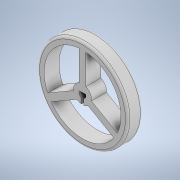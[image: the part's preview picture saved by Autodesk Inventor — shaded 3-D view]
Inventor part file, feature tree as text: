
AUTODESK INVENTOR PART (.ipt)
format: ipt  version: 2022.2 (Build 262287010, 287A)  size: 186,880 bytes
history: native  units: mm
features: extrude x4, sketch x4, fillet x1
ambient origin geometry x8: Origin, YZ Plane, XZ Plane, XY Plane, X Axis, Y Axis, Z Axis, Center Point
bodies: Solid1 (feature_tree)
feature tree (9):
  extrude  "Extrusion1"  Depth=6.6mm TaperAngle=0.0deg
  extrude  "Extrusion3"  TaperAngle=120.0deg  [1 undecoded]
  extrude  "Extrusion5"  Depth=1.5mm
  extrude  "Extrusion6"  Depth=1.5mm
  fillet  "Arredondamento1"  Radius=1.5mm
  sketch  "Sketch1"  dims[d0=40.0mm d1=6.6mm d2=0.0mm]
  sketch  "Sketch3"  dims[d6=34.0mm d7=120.0deg]
  sketch  "Sketch5"  dims[d8=150.0deg d9=1.5mm]
  sketch  "Sketch6"  dims[d10=1.5mm d11=1.5mm d12=1.5mm d13=1.5mm d14=1.5mm d15=2.0mm d16=0.0mm d20=8.0mm d21=6.6mm d22=0.0mm d23=3.0mm d24=0.5mm d25=0.5mm d27=10.0mm d28=0.0mm d29=2.2mm d30=1.0mm d26=0.5mm]
note: 1 required parameter value undecoded (feature->parameter linkage not recoverable at this tier; creation-order binding heuristic only, values carry confidence <= 0.55)
